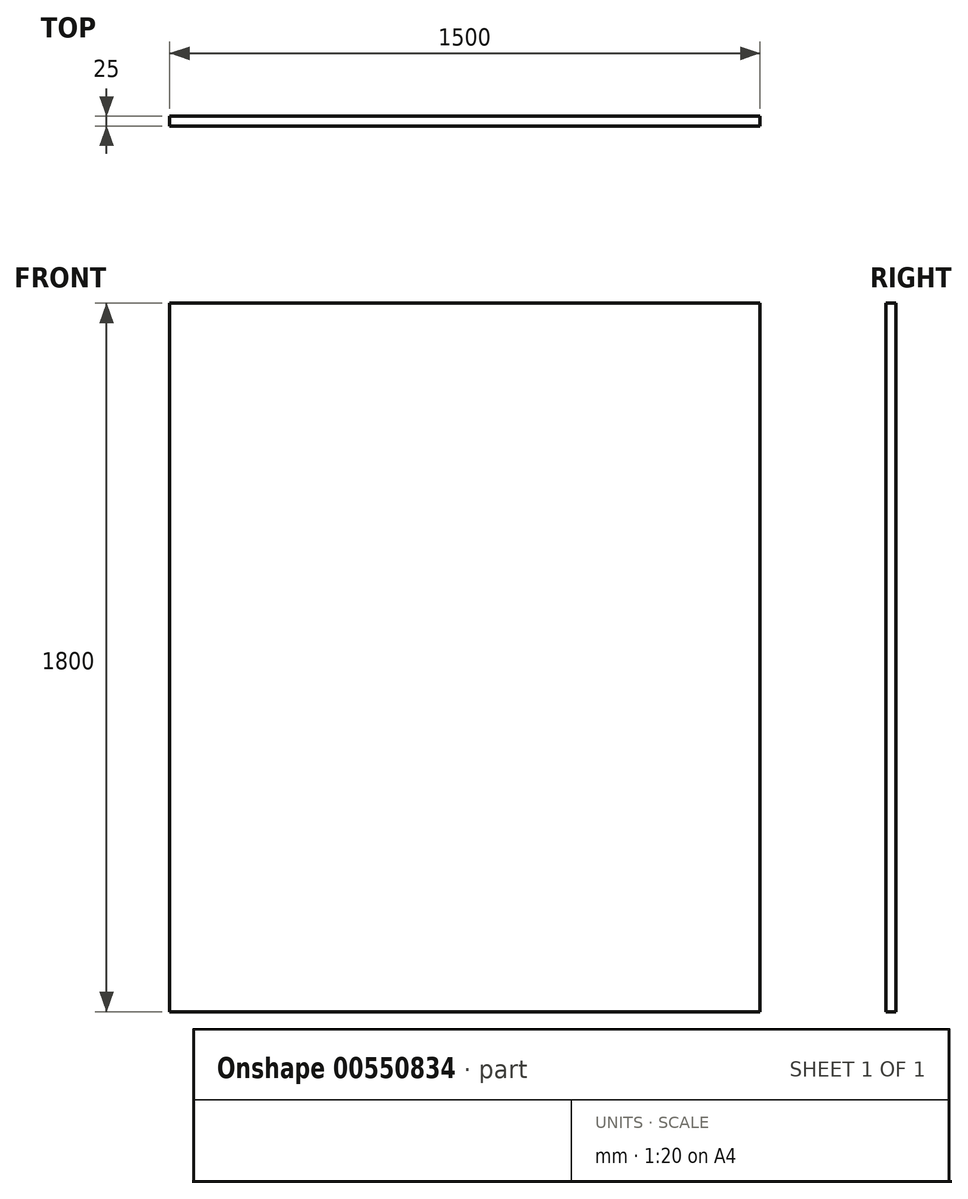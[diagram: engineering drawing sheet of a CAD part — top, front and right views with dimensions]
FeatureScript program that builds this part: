
annotation { "Feature Type Name" : "Feature", "Feature Type Description" : "" }
export const myFeature = defineFeature(function(context is Context, id is Id, definition is map)
    precondition{}
    {
        {
            var Q0;
            Q0=qCreatedBy(makeId("Front.planeOp"),FACE);
            var sketch = newSketch(context, id + "F0", { "sketchPlane" : qUnion([Q0])});
            skLineSegment(sketch, "E0.bottom", {"start": v(-51.34, 1740.66) * mm, "end": v(1448.66, 1740.66) * mm});
            skLineSegment(sketch, "E0.top", {"start": v(-51.34, -59.34) * mm, "end": v(1448.66, -59.34) * mm});
            skLineSegment(sketch, "E0.left", {"start": v(-51.34, 1740.66) * mm, "end": v(-51.34, -59.34) * mm});
            skLineSegment(sketch, "E0.right", {"start": v(1448.66, 1740.66) * mm, "end": v(1448.66, -59.34) * mm});
            skSolve(sketch);
        }
        {
            var Q0;
            Q0 = qSketchRegion(id + "F0", true);
            extrude(context, id + "F1", {"entities" : qUnion([Q0]), "depth" : 25 * mm, "offsetDistance" : 25 * mm});
        }
    });
